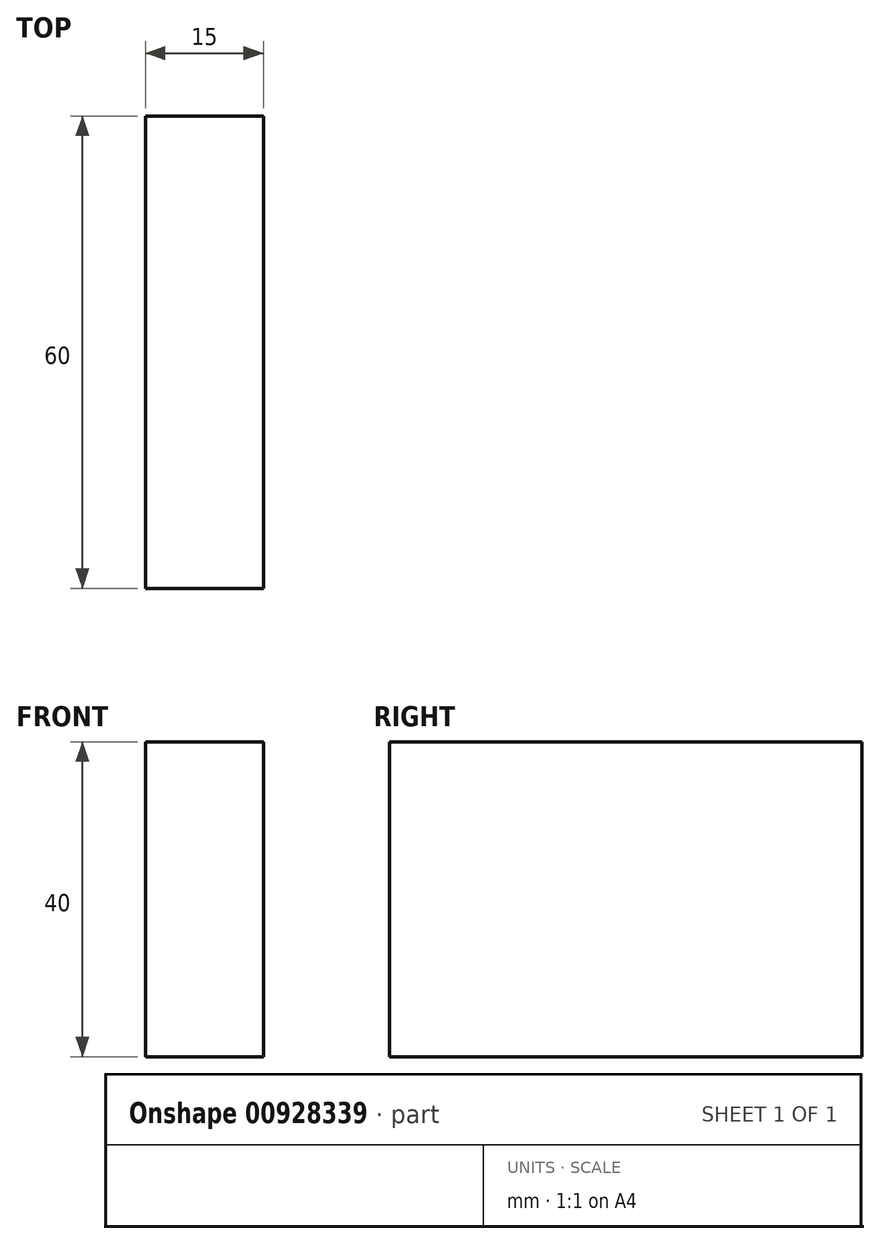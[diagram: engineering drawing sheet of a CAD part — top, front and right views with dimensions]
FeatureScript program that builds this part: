
annotation { "Feature Type Name" : "Feature", "Feature Type Description" : "" }
export const myFeature = defineFeature(function(context is Context, id is Id, definition is map)
    precondition{}
    {
        {
            var Q0;
            Q0=qCreatedBy(makeId("Top.planeOp"),FACE);
            var sketch = newSketch(context, id + "F0", { "sketchPlane" : qUnion([Q0])});
            skLineSegment(sketch, "E0.bottom", {"start": v(7.5, 30) * mm, "end": v(-7.5, 30) * mm});
            skLineSegment(sketch, "E0.top", {"start": v(7.5, -30) * mm, "end": v(-7.5, -30) * mm});
            skLineSegment(sketch, "E0.left", {"start": v(7.5, 30) * mm, "end": v(7.5, -30) * mm});
            skLineSegment(sketch, "E0.right", {"start": v(-7.5, 30) * mm, "end": v(-7.5, -30) * mm});
            skPoint(sketch, "E0.middle", {"position": v(0, 0) * mm});
            skSolve(sketch);
        }
        {
            var Q0;
            Q0=makeQuery(id+"F0.imprint","IMPRINT",FACE,{"disambiguationData":[TD([[makeQuery(id+"F0.imprint","IMPRINT",EDGE,{"derivedFrom":sQuery(id+"F0.wireOp",EDGE,"E0.bottom")}),1.0]])]});
            extrude(context, id + "F1", {"entities" : qUnion([Q0]), "depth" : -40 * mm, "offsetDistance" : 25 * mm});
        }
    });
